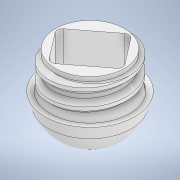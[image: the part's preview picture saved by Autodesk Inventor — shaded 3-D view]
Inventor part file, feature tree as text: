
AUTODESK INVENTOR PART (.ipt)
format: ipt  version: 2020 (Build 240168000, 168)  size: 729,600 bytes
history: native  units: in
note: dims shown in document units (in); Inventor stores cm internally (conversion verified against a paired STEP export)
features: other x6, sketch x5, thread x2, revolve x2, helix x2, emboss x2, shell x1, boolean_combine x1, extrude x1
ambient origin geometry x8: Origin, YZ Plane, XZ Plane, XY Plane, X Axis, Y Axis, Z Axis, Center Point
bodies: Solid1 (feature_tree), Solid2 (feature_tree), Solid3 (feature_tree)
feature tree (22):
  other  "SmartEgg Housing Main.ipt"
  other  "SmartEgg Housing Cap.ipt"
  shell  "Shell Sketch"  Thickness=0.3937in
  thread  "Thread Sketch"  [1 undecoded]
  revolve  "Revolution1"  [1 undecoded]
  helix  "Coil1"  [1 undecoded]
  helix  "Coil2"  [1 undecoded]
  thread  "Thread Mask"  [1 undecoded]
  revolve  "Revolution4"  [1 undecoded]
  boolean_combine  "Combine1"
  sketch  "Sketch10"  dims[d23=0.0787in d24=0.4921in]
  sketch  "Sketch11"  dims[d25=0.0098in d26=0.7874in]
  extrude  "Extrusion1"  Depth=0.7874in
  other  "Vent Lookup"
  other  "Vent Plane"
  emboss  "Emboss1"
  emboss  "Emboss2"
  sketch  "Sketch3"  dims[d18=0.9843in d19=1.9685in d20=0.0394in d21=0.6693in d22=0.1969in]
  other  "Housing Largest Area"
  other  "ESP32 Feather"
  sketch  "Sketch13"  dims[d27=0.1181in]
  sketch  "Sketch14"  dims[d28=0.0787in d29=2.7769in d30=0.0394in d32=0.0197in d33=0.0197in d35=45.0deg d36=0.0197in d37=0.0787in d38=0.0787in d39=0.2756in d40=90.0deg d41=0.3706in d42=0.3937in d43=1.1811in d44=0.0in d45=90.0deg d46=90.0deg d47=0.0in d48=0.0in d50=0.3706in d51=0.3937in d52=0.3937in d53=0.0in d54=90.0deg d55=90.0deg d56=0.0in d57=0.0in d61=0.0984in d62=90.0deg d64=0.0148in d65=1.2106in d66=0.1181in d67=1.3976in d68=1.3976in d69=0.0in d71=0.2559in d72=1.9488in d73=0.0154in d74=0.0in d75=0.0787in d76=0.0787in d77=0.0787in d78=0.0394in d79=0.0in d89=0.1969in d90=60.0deg]
note: 6 required parameter values undecoded (feature->parameter linkage not recoverable at this tier; creation-order binding heuristic only, values carry confidence <= 0.55)